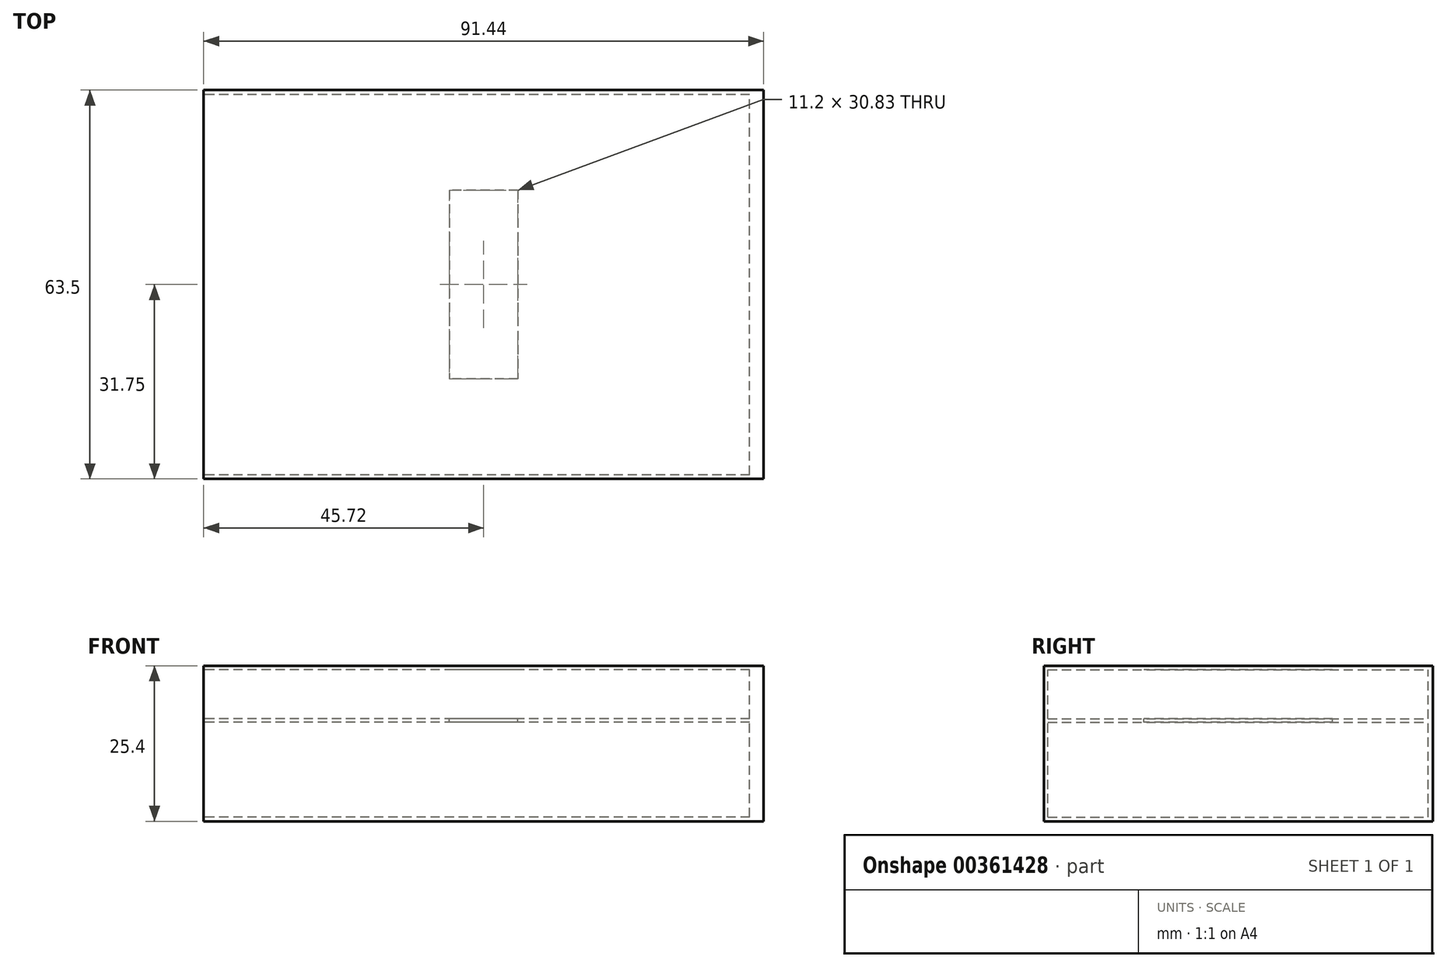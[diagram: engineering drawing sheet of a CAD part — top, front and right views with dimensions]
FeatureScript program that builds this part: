
annotation { "Feature Type Name" : "Feature", "Feature Type Description" : "" }
export const myFeature = defineFeature(function(context is Context, id is Id, definition is map)
    precondition{}
    {
        {
            var Q0;
            Q0=qCreatedBy(makeId("Top.planeOp"),FACE);
            var sketch = newSketch(context, id + "F0", { "sketchPlane" : qUnion([Q0])});
            skLineSegment(sketch, "E0.bottom", {"start": v(45.72, 31.75) * mm, "end": v(-45.72, 31.75) * mm});
            skLineSegment(sketch, "E0.top", {"start": v(45.72, -31.75) * mm, "end": v(-45.72, -31.75) * mm});
            skLineSegment(sketch, "E0.left", {"start": v(45.72, 31.75) * mm, "end": v(45.72, -31.75) * mm});
            skLineSegment(sketch, "E0.right", {"start": v(-45.72, 31.75) * mm, "end": v(-45.72, -31.75) * mm});
            skPoint(sketch, "E0.middle", {"position": v(0, 0) * mm});
            skSolve(sketch);
        }
        {
            var Q0;
            Q0 = qSketchRegion(id + "F0", true);
            extrude(context, id + "F1", {"entities" : qUnion([Q0]), "depth" : 25.4 * mm});
        }
        {
            var Q0;
            Q0=makeQuery(id+"F1.opExtrude","SWEPT_FACE",FACE,{"disambiguationData":[OSD([sQuery(id+"F0.wireOp",EDGE,"E0.right")])]});
            var sketch = newSketch(context, id + "F2", { "sketchPlane" : qUnion([Q0])});
            skSolve(sketch);
        }
        {
            var Q0;
            {var subQ0=sQuery(id+"F0.wireOp",EDGE,"E0.right");Q0=makeQuery(id+"F2.imprint","IMPRINT",FACE,{"disambiguationData":[TD([[makeQuery(id+"F2.imprint","IMPRINT",EDGE,{"derivedFrom":makeQuery(id+"F1.opExtrude","CAP_EDGE",EDGE,{"disambiguationData":[OSD([subQ0])],"isStart":true})}),1.0]])]});}
            var sketch = newSketch(context, id + "F3", { "sketchPlane" : qUnion([Q0])});
            skLineSegment(sketch, "E1.bottom", {"start": v(31.07, 0.67) * mm, "end": v(-31.04, 0.67) * mm});
            skLineSegment(sketch, "E1.top", {"start": v(31.07, 24.75) * mm, "end": v(-31.04, 24.75) * mm});
            skLineSegment(sketch, "E1.left", {"start": v(31.07, 0.67) * mm, "end": v(31.07, 24.75) * mm});
            skLineSegment(sketch, "E1.right", {"start": v(-31.04, 0.67) * mm, "end": v(-31.04, 24.75) * mm});
            skSolve(sketch);
        }
        {
            var Q0;
            Q0 = qSketchRegion(id + "F3", true);
            extrude(context, id + "F4", {"entities" : qUnion([Q0]), "operationType" : NewBodyOperationType.REMOVE, "oppositeDirection" : true, "depth" : 89.15 * mm});
        }
        {
            var Q0;
            Q0=makeQuery(id+"F1.opExtrude","SWEPT_FACE",FACE,{"disambiguationData":[OSD([sQuery(id+"F0.wireOp",EDGE,"E0.top")])]});
            var sketch = newSketch(context, id + "F5", { "sketchPlane" : qUnion([Q0])});
            skLineSegment(sketch, "E2.bottom", {"start": v(45.72, 16.77) * mm, "end": v(-45.72, 16.77) * mm});
            skLineSegment(sketch, "E2.top", {"start": v(45.72, 16.19) * mm, "end": v(-45.72, 16.19) * mm});
            skLineSegment(sketch, "E2.left", {"start": v(45.72, 16.77) * mm, "end": v(45.72, 16.19) * mm});
            skLineSegment(sketch, "E2.right", {"start": v(-45.72, 16.77) * mm, "end": v(-45.72, 16.19) * mm});
            skSolve(sketch);
        }
        {
            var Q0;
            Q0 = qSketchRegion(id + "F5", true);
            extrude(context, id + "F6", {"entities" : qUnion([Q0]), "operationType" : NewBodyOperationType.ADD, "oppositeDirection" : true, "depth" : 63.22 * mm});
        }
        {
            var Q0;
            Q0=makeQuery(id+"F1.opExtrude","CAP_FACE",FACE,{"disambiguationData":[OSD([sQuery(id+"F0.wireOp",EDGE,"E0.bottom"),sQuery(id+"F0.wireOp",EDGE,"E0.top"),sQuery(id+"F0.wireOp",EDGE,"E0.left"),sQuery(id+"F0.wireOp",EDGE,"E0.right")])],"isStart":false});
            var sketch = newSketch(context, id + "F7", { "sketchPlane" : qUnion([Q0])});
            skLineSegment(sketch, "E3.bottom", {"start": v(5.6, 15.41) * mm, "end": v(-5.6, 15.41) * mm});
            skLineSegment(sketch, "E3.top", {"start": v(5.6, -15.41) * mm, "end": v(-5.6, -15.41) * mm});
            skLineSegment(sketch, "E3.left", {"start": v(5.6, 15.41) * mm, "end": v(5.6, -15.41) * mm});
            skLineSegment(sketch, "E3.right", {"start": v(-5.6, 15.41) * mm, "end": v(-5.6, -15.41) * mm});
            skPoint(sketch, "E3.middle", {"position": v(0, 0) * mm});
            skSolve(sketch);
        }
        {
            var Q0;
            Q0 = qSketchRegion(id + "F7", true);
            extrude(context, id + "F8", {"entities" : qUnion([Q0]), "operationType" : NewBodyOperationType.REMOVE, "oppositeDirection" : true, "depth" : 15.24 * mm});
        }
        {
            var Q0;
            Q0=makeQuery(id+"F1.opExtrude","CAP_FACE",FACE,{"disambiguationData":[OSD([sQuery(id+"F0.wireOp",EDGE,"E0.bottom"),sQuery(id+"F0.wireOp",EDGE,"E0.top"),sQuery(id+"F0.wireOp",EDGE,"E0.left"),sQuery(id+"F0.wireOp",EDGE,"E0.right")])],"isStart":false});
            var sketch = newSketch(context, id + "F9", { "sketchPlane" : qUnion([Q0])});
            skLineSegment(sketch, "E4.bottom", {"start": v(-5.6, 15.41) * mm, "end": v(5.6, 15.41) * mm});
            skLineSegment(sketch, "E4.top", {"start": v(-5.6, -15.41) * mm, "end": v(5.6, -15.41) * mm});
            skLineSegment(sketch, "E4.left", {"start": v(-5.6, 15.41) * mm, "end": v(-5.6, -15.41) * mm});
            skLineSegment(sketch, "E4.right", {"start": v(5.6, 15.41) * mm, "end": v(5.6, -15.41) * mm});
            skPoint(sketch, "E4.middle", {"position": v(0, 0) * mm});
            skSolve(sketch);
        }
        {
            var Q0;
            Q0 = qSketchRegion(id + "F9", true);
            extrude(context, id + "F10", {"entities" : qUnion([Q0]), "operationType" : NewBodyOperationType.ADD, "oppositeDirection" : true, "depth" : 0.63 * mm});
        }
    });
